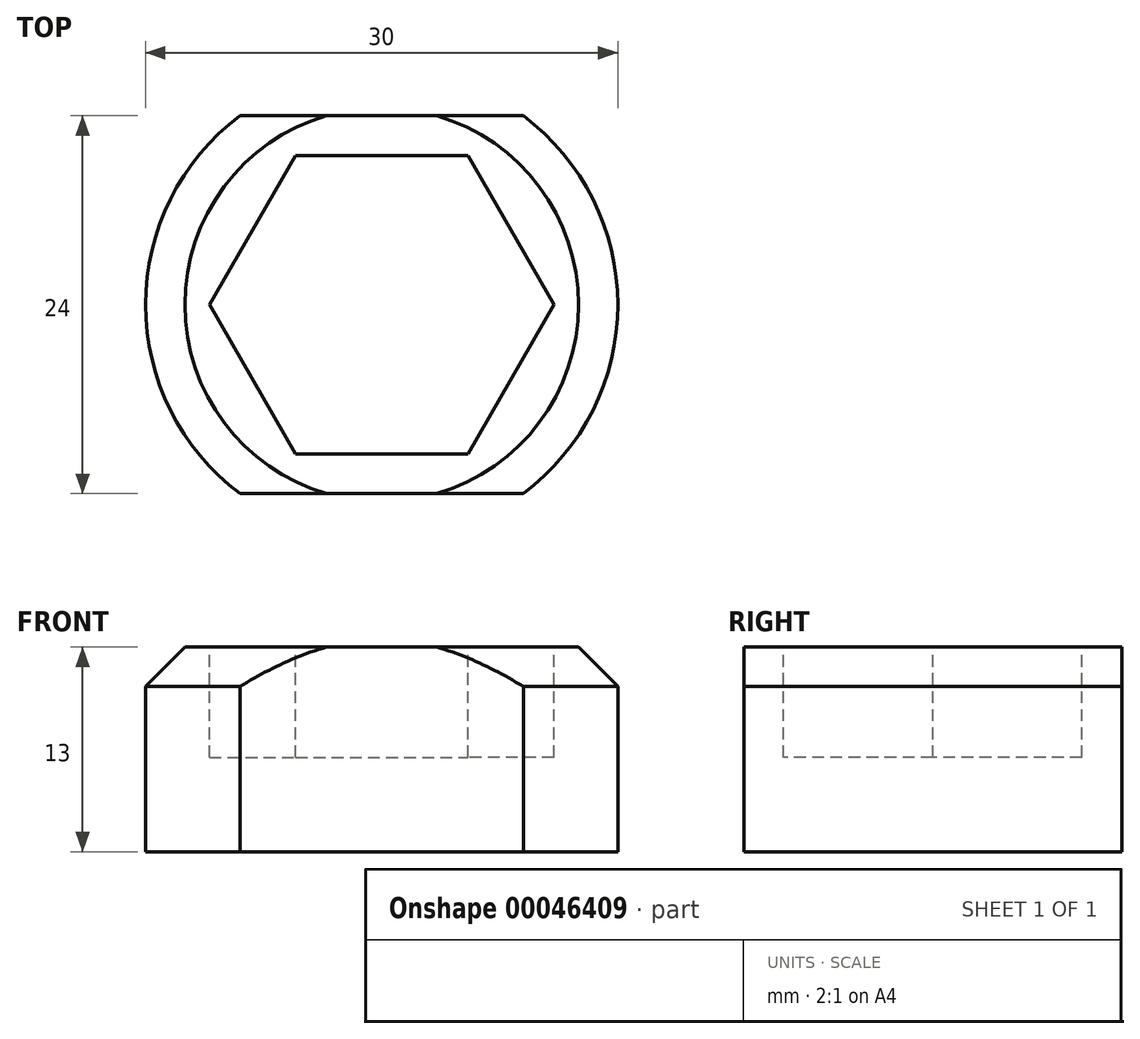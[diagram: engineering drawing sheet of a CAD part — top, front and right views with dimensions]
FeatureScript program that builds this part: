
annotation { "Feature Type Name" : "Feature", "Feature Type Description" : "" }
export const myFeature = defineFeature(function(context is Context, id is Id, definition is map)
    precondition{}
    {
        {
            var Q0;
            Q0=qCreatedBy(makeId("Top.planeOp"),FACE);
            var sketch = newSketch(context, id + "F0", { "sketchPlane" : qUnion([Q0])});
            skCircle(sketch, "E0", {"center": v(0, 0) * mm, "radius": 15 * mm});
            skLineSegment(sketch, "E1", {"start": v(-9, -12) * mm, "end": v(9, -12) * mm});
            skLineSegment(sketch, "E2.MirrorCS", {"start": v(-9, 12) * mm, "end": v(9, 12) * mm});
            skSolve(sketch);
        }
        {
            var Q0;
            Q0=makeQuery(id+"F0.imprint","IMPRINT",FACE,{"disambiguationData":[TD([[makeQuery(id+"F0.imprint","IMPRINT",EDGE,{"derivedFrom":sQuery(id+"F0.wireOp",EDGE,"E0")}),1.0]])]});
            extrude(context, id + "F1", {"entities" : qUnion([Q0]), "depth" : 13 * mm, "offsetDistance" : 25 * mm});
        }
        {
            var Q0;
            Q0=makeQuery(id+"F1.opExtrude","CAP_FACE",FACE,{"disambiguationData":[OSD([sQuery(id+"F0.wireOp",EDGE,"E0"),sQuery(id+"F0.wireOp",EDGE,"E1"),sQuery(id+"F0.wireOp",EDGE,"E2.MirrorCS")])],"isStart":false});
            var sketch = newSketch(context, id + "F2", { "sketchPlane" : qUnion([Q0])});
            skCircle(sketch, "E3.cCircle", {"center": v(0, 0) * mm, "radius": 9.47 * mm, "construction": true});
            skLineSegment(sketch, "E3.0", {"start": v(10.94, 0) * mm, "end": v(5.47, -9.48) * mm});
            skLineSegment(sketch, "E3.1", {"start": v(5.47, -9.48) * mm, "end": v(-5.47, -9.48) * mm});
            skLineSegment(sketch, "E3.2", {"start": v(-5.47, -9.48) * mm, "end": v(-10.94, 0) * mm});
            skLineSegment(sketch, "E3.3", {"start": v(-10.94, 0) * mm, "end": v(-5.47, 9.47) * mm});
            skLineSegment(sketch, "E3.4", {"start": v(-5.47, 9.47) * mm, "end": v(5.47, 9.47) * mm});
            skLineSegment(sketch, "E3.5", {"start": v(5.47, 9.47) * mm, "end": v(10.94, 0) * mm});
            skPoint(sketch, "E3.0.midPoint", {"position": v(8.2, -4.74) * mm});
            skSolve(sketch);
        }
        {
            var Q0;
            Q0=makeQuery(id+"F2.imprint","IMPRINT",FACE,{"disambiguationData":[TD([[makeQuery(id+"F2.imprint","IMPRINT",EDGE,{"derivedFrom":sQuery(id+"F2.wireOp",EDGE,"E3.0")}),-1.0]])]});
            extrude(context, id + "F3", {"entities" : qUnion([Q0]), "operationType" : NewBodyOperationType.REMOVE, "oppositeDirection" : true, "depth" : 7 * mm, "offsetDistance" : 25 * mm});
        }
        {
            var Q0;
            {var subQ0=sQuery(id+"F0.wireOp",EDGE,"E0");Q0=makeQuery(id+"F1.opExtrude","CAP_EDGE",EDGE,{"disambiguationData":[OSD([subQ0]),TDD([makeQuery(id+"F0.imprint","IMPRINT",EDGE,{"disambiguationData":[TD([[makeQuery(id+"F0.imprint","INTERSECT",VERTEX,{"disambiguationData":[OD(1.0)],"derivedFrom":[subQ0,sQuery(id+"F0.wireOp",EDGE,"E1")]}),-1.0]])],"derivedFrom":subQ0})])],"isStart":false});}
            var Q1;
            {var subQ0=sQuery(id+"F0.wireOp",EDGE,"E0");Q1=makeQuery(id+"F1.opExtrude","CAP_EDGE",EDGE,{"disambiguationData":[OSD([subQ0]),TDD([makeQuery(id+"F0.imprint","IMPRINT",EDGE,{"disambiguationData":[TD([[makeQuery(id+"F0.imprint","INTERSECT",VERTEX,{"disambiguationData":[OD(0.0)],"derivedFrom":[subQ0,sQuery(id+"F0.wireOp",EDGE,"E1")]}),1.0]])],"derivedFrom":subQ0})])],"isStart":false});}
            chamfer(context, id + "F4", {"entities" : qUnion([Q0, Q1]), "width" : 2.5 * mm, "tangentPropagation" : true});
        }
        {
            var Q0;
            {var subQ1=sQuery(id+"F0.wireOp",EDGE,"E1");Q0=makeQuery(id+"F0.imprint","IMPRINT",FACE,{"disambiguationData":[TD([[makeQuery(id+"F0.imprint","IMPRINT",EDGE,{"derivedFrom":subQ1}),1.0]])]});}
            var Q1;
            Q1=makeQuery(id+"F0.imprint","IMPRINT",FACE,{"disambiguationData":[TD([[makeQuery(id+"F0.imprint","IMPRINT",EDGE,{"derivedFrom":sQuery(id+"F0.wireOp",EDGE,"fPqL4YEt-MZ4W-SnuZ-cGuZ-N1o7cRGL11Mw")}),1.0]])]});
            extrude(context, id + "F5", {"entities" : qUnion([Q0, Q1]), "operationType" : NewBodyOperationType.ADD, "depth" : 2 * mm, "offsetDistance" : 25 * mm});
        }
    });
